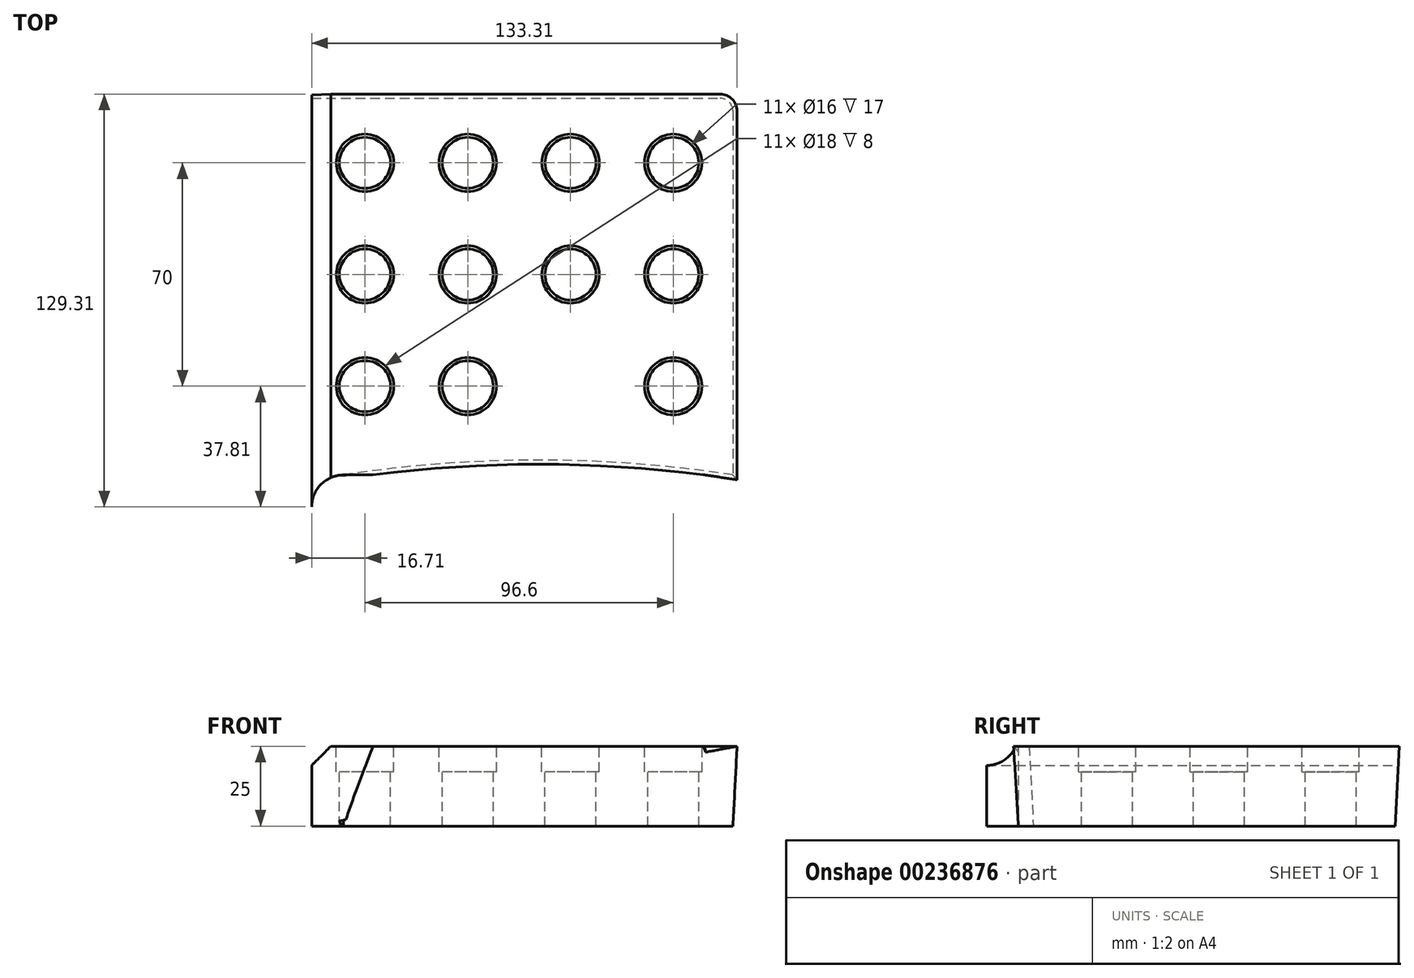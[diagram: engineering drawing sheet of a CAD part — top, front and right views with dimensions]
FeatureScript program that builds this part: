
annotation { "Feature Type Name" : "Feature", "Feature Type Description" : "" }
export const myFeature = defineFeature(function(context is Context, id is Id, definition is map)
    precondition{}
    {
        {
            var Q0;
            Q0=qCreatedBy(makeId("Top.planeOp"),FACE);
            var sketch = newSketch(context, id + "F0", { "sketchPlane" : qUnion([Q0])});
            skLineSegment(sketch, "E0.bottom", {"start": v(0, 0) * mm, "end": v(10, 0) * mm});
            skLineSegment(sketch, "E0.top", {"start": v(0, 118) * mm, "end": v(128, 118) * mm});
            skLineSegment(sketch, "E0.left", {"start": v(0, 0) * mm, "end": v(0, 118) * mm});
            skLineSegment(sketch, "E0.right", {"start": v(132, 0) * mm, "end": v(132, 114) * mm});
            skPoint(sketch, "E1.visualSharp", {"position": v(132, 118) * mm});
            skArc(sketch, "E1.filletArc", {"start": v(132, 114) * mm, "mid": v(130.83, 116.83) * mm, "end": v(128, 118) * mm});
            skLineSegment(sketch, "E2", {"start": v(0, 0) * mm, "end": v(10, 0) * mm, "construction": true});
            skArc(sketch, "E3", {"start": v(132, 0) * mm, "mid": v(71, 4.68) * mm, "end": v(10, 0) * mm});
            skSolve(sketch);
        }
        {
            var Q0;
            Q0 = qSketchRegion(id + "F0", true);
            extrude(context, id + "F1", {"entities" : qUnion([Q0]), "depth" : 25 * mm, "hasDraft" : true, "draftAngle" : 3 * degree});
        }
        {
            var Q0;
            Q0=qCreatedBy(makeId("Front.planeOp"),FACE);
            var sketch = newSketch(context, id + "F2", { "sketchPlane" : qUnion([Q0])});
            skLineSegment(sketch, "E4.0.0", {"start": v(0, 0) * mm, "end": v(0, 0) * mm});
            skLineSegment(sketch, "E4.0.1", {"start": v(0, 0) * mm, "end": v(133.31, 25) * mm});
            skLineSegment(sketch, "E4.0.2", {"start": v(-1.31, 25) * mm, "end": v(133.31, 25) * mm});
            skLineSegment(sketch, "E4.0.3", {"start": v(-1.31, 25) * mm, "end": v(0, 0) * mm});
            skSolve(sketch);
        }
        {
            var Q0;
            Q0 = qSketchRegion(id + "F2", true);
            extrude(context, id + "F3", {"entities" : qUnion([Q0]), "operationType" : NewBodyOperationType.REMOVE, "endBound" : BoundingType.THROUGH_ALL, "depth" : 25 * mm});
        }
        {
            var Q0;
            Q0=qCreatedBy(makeId("Right.planeOp"),FACE);
            var sketch = newSketch(context, id + "F4", { "sketchPlane" : qUnion([Q0])});
            skLineSegment(sketch, "E5.0.0", {"start": v(0, 0) * mm, "end": v(0, 25) * mm});
            skLineSegment(sketch, "E5.0.1", {"start": v(0, 25) * mm, "end": v(119.31, 25) * mm});
            skLineSegment(sketch, "E5.0.2", {"start": v(119.31, 25) * mm, "end": v(118, 0) * mm});
            skLineSegment(sketch, "E5.0.3", {"start": v(118, 0) * mm, "end": v(0, 0) * mm});
            skSolve(sketch);
        }
        {
            var Q0;
            Q0 = qSketchRegion(id + "F4", true);
            extrude(context, id + "F5", {"entities" : qUnion([Q0]), "operationType" : NewBodyOperationType.REMOVE, "endBound" : BoundingType.THROUGH_ALL, "oppositeDirection" : true, "depth" : 25 * mm});
        }
        {
            var Q0;
            Q0=qCreatedBy(makeId("Top.planeOp"),FACE);
            var sketch = newSketch(context, id + "F6", { "sketchPlane" : qUnion([Q0])});
            skLineSegment(sketch, "E6.bottom", {"start": v(10, 0) * mm, "end": v(10, 0) * mm});
            skLineSegment(sketch, "E6.left", {"start": v(0, -10) * mm, "end": v(0, -10) * mm});
            skPoint(sketch, "E7.visualSharp", {"position": v(0, 0) * mm});
            skArc(sketch, "E7.filletArc", {"start": v(10, 0) * mm, "mid": v(2.93, -2.93) * mm, "end": v(0, -10) * mm});
            skLineSegment(sketch, "E8", {"start": v(0, -10) * mm, "end": v(0, 0) * mm});
            skLineSegment(sketch, "E9", {"start": v(0, 0) * mm, "end": v(10, 0) * mm});
            skSolve(sketch);
        }
        {
            var Q0;
            Q0 = qSketchRegion(id + "F6", true);
            extrude(context, id + "F7", {"entities" : qUnion([Q0]), "operationType" : NewBodyOperationType.ADD, "depth" : 25 * mm});
        }
        {
            var Q0;
            Q0=makeQuery(id+"F7.boolean.opBoolean","MERGE",EDGE,{"derivedFrom":[makeQuery(id+"F5.boolean.opBoolean","COPY",EDGE,{"derivedFrom":makeQuery(id+"F5.opExtrude","CAP_EDGE",EDGE,{"disambiguationData":[OSD([sQuery(id+"F4.wireOp",EDGE,"E5.0.1")])],"isStart":true})}),makeQuery(id+"F7.opExtrude","CAP_EDGE",EDGE,{"disambiguationData":[OSD([sQuery(id+"F6.wireOp",EDGE,"E8")])],"isStart":false})]});
            chamfer(context, id + "F8", {"entities" : qUnion([Q0]), "width" : 6 * mm, "tangentPropagation" : true});
        }
        {
            var Q0;
            {var subQ1=sQuery(id+"F0.wireOp",EDGE,"E0.right");var subQ2=sQuery(id+"F2.wireOp",EDGE,"E4.0.1");Q0=makeQuery(id+"F3.boolean.opBoolean","COPY",FACE,{"disambiguationData":[TD([makeQuery(id+"F1.opExtrude","SWEPT_FACE",FACE,{"disambiguationData":[OSD([subQ1])]})])],"derivedFrom":makeQuery(id+"F3.opExtrude","SWEPT_FACE",FACE,{"disambiguationData":[OSD([subQ2])]})});}
            var sketch = newSketch(context, id + "F9", { "sketchPlane" : qUnion([Q0])});
            skLineSegment(sketch, "E10.0.0", {"start": v(135.63, -1.53) * mm, "end": v(135.63, 0) * mm});
            skLineSegment(sketch, "E10.0.1", {"start": v(135.63, 0) * mm, "end": v(125.6, 0) * mm});
            skEllipticalArc(sketch, "E10.0.2", {});
            const initialGuessF9  = {"E10.0.2": [0.06824448755918142, -0.39532138823999896, -1, 0, 0.40630219611644297, 0.39932148659949984, 4.545758140319845, 4.5707273626514375]};
            skSetInitialGuess(sketch, initialGuessF9);
            skSolve(sketch);
        }
        {
            var Q0;
            Q0 = qSketchRegion(id + "F9", true);
            var Q1;
            Q1=makeQuery(id+"F7.boolean.opBoolean","MERGE",FACE,{"derivedFrom":[makeQuery(id+"F1.opExtrude","CAP_FACE",FACE,{"disambiguationData":[OSD([sQuery(id+"F0.wireOp",EDGE,"E0.bottom"),sQuery(id+"F0.wireOp",EDGE,"E0.top"),sQuery(id+"F0.wireOp",EDGE,"E0.left"),sQuery(id+"F0.wireOp",EDGE,"E0.right"),sQuery(id+"F0.wireOp",EDGE,"E1.filletArc"),sQuery(id+"F0.wireOp",EDGE,"E3")])],"isStart":false}),makeQuery(id+"F7.opExtrude","CAP_FACE",FACE,{"disambiguationData":[OSD([sQuery(id+"F6.wireOp",EDGE,"E7.filletArc"),sQuery(id+"F6.wireOp",EDGE,"E8"),sQuery(id+"F6.wireOp",EDGE,"E9")])],"isStart":false})]});
            extrude(context, id + "F10", {"entities" : qUnion([Q0]), "operationType" : NewBodyOperationType.ADD, "endBound" : BoundingType.UP_TO_SURFACE, "endBoundEntityFace" : qUnion([Q1]), "depth" : 25 * mm, "offsetDistance" : 25 * mm});
        }
        {
            var Q0;
            Q0=makeQuery(id+"F7.boolean.opBoolean","MERGE",FACE,{"derivedFrom":[makeQuery(id+"F1.opExtrude","CAP_FACE",FACE,{"disambiguationData":[OSD([sQuery(id+"F0.wireOp",EDGE,"E0.bottom"),sQuery(id+"F0.wireOp",EDGE,"E0.top"),sQuery(id+"F0.wireOp",EDGE,"E0.left"),sQuery(id+"F0.wireOp",EDGE,"E0.right"),sQuery(id+"F0.wireOp",EDGE,"E1.filletArc")])],"isStart":false}),makeQuery(id+"F7.opExtrude","CAP_FACE",FACE,{"disambiguationData":[OSD([sQuery(id+"F6.wireOp",EDGE,"E7.filletArc"),sQuery(id+"F6.wireOp",EDGE,"E8"),sQuery(id+"F6.wireOp",EDGE,"E9")])],"isStart":false})]});
            var sketch = newSketch(context, id + "F11", { "sketchPlane" : qUnion([Q0])});
            skLineSegment(sketch, "E11", {"start": v(128, 119.31) * mm, "end": v(139.92, 119.31) * mm, "construction": true});
            skLineSegment(sketch, "E12", {"start": v(139.92, 119.31) * mm, "end": v(133.31, 114) * mm, "construction": true});
            skLineSegment(sketch, "E13", {"start": v(133.31, 114) * mm, "end": v(133.31, 119.31) * mm, "construction": true});
            skLineSegment(sketch, "E14.bottom", {"start": v(133.31, 119.31) * mm, "end": v(113.31, 119.31) * mm, "construction": true});
            skLineSegment(sketch, "E14.top", {"start": v(133.31, 97.81) * mm, "end": v(113.31, 97.81) * mm, "construction": true});
            skLineSegment(sketch, "E14.left", {"start": v(133.31, 119.31) * mm, "end": v(133.31, 97.81) * mm, "construction": true});
            skLineSegment(sketch, "E14.right", {"start": v(113.31, 119.31) * mm, "end": v(113.31, 97.81) * mm, "construction": true});
            skLineSegment(sketch, "E15.bottom", {"start": v(113.31, 97.81) * mm, "end": v(81.11, 97.81) * mm, "construction": true});
            skLineSegment(sketch, "E15.top", {"start": v(113.31, 62.81) * mm, "end": v(81.11, 62.81) * mm, "construction": true});
            skLineSegment(sketch, "E15.left", {"start": v(113.31, 97.81) * mm, "end": v(113.31, 62.81) * mm, "construction": true});
            skLineSegment(sketch, "E15.right", {"start": v(81.11, 97.81) * mm, "end": v(81.11, 62.81) * mm, "construction": true});
            skLineSegment(sketch, "E16.bottom", {"start": v(81.11, 97.81) * mm, "end": v(48.91, 97.81) * mm, "construction": true});
            skLineSegment(sketch, "E16.top", {"start": v(81.11, 62.81) * mm, "end": v(48.91, 62.81) * mm, "construction": true});
            skLineSegment(sketch, "E16.right", {"start": v(48.91, 97.81) * mm, "end": v(48.91, 62.81) * mm, "construction": true});
            skLineSegment(sketch, "E17.bottom", {"start": v(48.91, 97.81) * mm, "end": v(16.71, 97.81) * mm, "construction": true});
            skLineSegment(sketch, "E17.top", {"start": v(48.91, 62.81) * mm, "end": v(16.71, 62.81) * mm, "construction": true});
            skLineSegment(sketch, "E17.right", {"start": v(16.71, 97.81) * mm, "end": v(16.71, 62.81) * mm, "construction": true});
            skLineSegment(sketch, "E18.bottom", {"start": v(16.71, 62.81) * mm, "end": v(16.71, 62.81) * mm});
            skLineSegment(sketch, "E18.top", {"start": v(16.71, 27.81) * mm, "end": v(16.71, 27.81) * mm});
            skLineSegment(sketch, "E18.left", {"start": v(16.71, 62.81) * mm, "end": v(16.71, 27.81) * mm, "construction": true});
            skLineSegment(sketch, "E18.right", {"start": v(16.71, 62.81) * mm, "end": v(16.71, 27.81) * mm, "construction": true});
            skLineSegment(sketch, "E19.bottom", {"start": v(113.31, 62.81) * mm, "end": v(48.91, 62.81) * mm, "construction": true});
            skLineSegment(sketch, "E19.top", {"start": v(113.31, 27.81) * mm, "end": v(48.91, 27.81) * mm, "construction": true});
            skLineSegment(sketch, "E19.right", {"start": v(48.91, 62.81) * mm, "end": v(48.91, 27.81) * mm, "construction": true});
            skCircle(sketch, "E20", {"center": v(16.71, 97.81) * mm, "radius": 8 * mm});
            skCircle(sketch, "E21", {"center": v(48.91, 97.81) * mm, "radius": 9 * mm});
            skCircle(sketch, "E22", {"center": v(81.11, 97.81) * mm, "radius": 9 * mm});
            skCircle(sketch, "E23", {"center": v(113.31, 97.81) * mm, "radius": 9 * mm});
            skCircle(sketch, "E24", {"center": v(113.31, 62.81) * mm, "radius": 9 * mm});
            skCircle(sketch, "E25", {"center": v(81.11, 62.81) * mm, "radius": 9 * mm});
            skCircle(sketch, "E26", {"center": v(48.91, 62.81) * mm, "radius": 9 * mm});
            skCircle(sketch, "E27", {"center": v(16.71, 62.81) * mm, "radius": 9 * mm});
            skCircle(sketch, "E28", {"center": v(16.71, 27.81) * mm, "radius": 9 * mm});
            skCircle(sketch, "E29", {"center": v(48.91, 27.81) * mm, "radius": 9 * mm});
            skCircle(sketch, "E30", {"center": v(48.91, 27.81) * mm, "radius": 8 * mm});
            skCircle(sketch, "E31", {"center": v(113.31, 62.81) * mm, "radius": 8 * mm});
            skCircle(sketch, "E32", {"center": v(81.11, 62.81) * mm, "radius": 8 * mm});
            skCircle(sketch, "E33", {"center": v(48.91, 62.81) * mm, "radius": 8 * mm});
            skCircle(sketch, "E34", {"center": v(16.71, 62.81) * mm, "radius": 8 * mm});
            skCircle(sketch, "E35", {"center": v(16.71, 27.81) * mm, "radius": 8 * mm});
            skCircle(sketch, "E36", {"center": v(48.91, 97.81) * mm, "radius": 8 * mm});
            skCircle(sketch, "E37", {"center": v(16.71, 97.81) * mm, "radius": 9 * mm});
            skCircle(sketch, "E38", {"center": v(81.11, 97.81) * mm, "radius": 8 * mm});
            skCircle(sketch, "E39", {"center": v(113.31, 97.81) * mm, "radius": 8 * mm});
            skCircle(sketch, "E40", {"center": v(113.31, 27.81) * mm, "radius": 9 * mm});
            skCircle(sketch, "E41", {"center": v(113.31, 27.81) * mm, "radius": 8 * mm});
            skSolve(sketch);
        }
        {
            var Q0;
            Q0=makeQuery(id+"F11.imprint","IMPRINT",FACE,{"disambiguationData":[TD([[makeQuery(id+"F11.imprint","IMPRINT",EDGE,{"derivedFrom":sQuery(id+"F11.wireOp",EDGE,"E36")}),1.0]])]});
            var Q1;
            Q1=makeQuery(id+"F11.imprint","IMPRINT",FACE,{"disambiguationData":[TD([[makeQuery(id+"F11.imprint","IMPRINT",EDGE,{"derivedFrom":sQuery(id+"F11.wireOp",EDGE,"E38")}),1.0]])]});
            var Q2;
            Q2=makeQuery(id+"F11.imprint","IMPRINT",FACE,{"disambiguationData":[TD([[makeQuery(id+"F11.imprint","IMPRINT",EDGE,{"derivedFrom":sQuery(id+"F11.wireOp",EDGE,"E39")}),1.0]])]});
            var Q3;
            Q3=makeQuery(id+"F11.imprint","IMPRINT",FACE,{"disambiguationData":[TD([[makeQuery(id+"F11.imprint","IMPRINT",EDGE,{"derivedFrom":sQuery(id+"F11.wireOp",EDGE,"E31")}),1.0]])]});
            var Q4;
            Q4=makeQuery(id+"F11.imprint","IMPRINT",FACE,{"disambiguationData":[TD([[makeQuery(id+"F11.imprint","IMPRINT",EDGE,{"derivedFrom":sQuery(id+"F11.wireOp",EDGE,"E32")}),1.0]])]});
            var Q5;
            Q5=makeQuery(id+"F11.imprint","IMPRINT",FACE,{"disambiguationData":[TD([[makeQuery(id+"F11.imprint","IMPRINT",EDGE,{"derivedFrom":sQuery(id+"F11.wireOp",EDGE,"E33")}),1.0]])]});
            var Q6;
            Q6=makeQuery(id+"F11.imprint","IMPRINT",FACE,{"disambiguationData":[TD([[makeQuery(id+"F11.imprint","IMPRINT",EDGE,{"derivedFrom":sQuery(id+"F11.wireOp",EDGE,"E34")}),1.0]])]});
            var Q7;
            Q7=makeQuery(id+"F11.imprint","IMPRINT",FACE,{"disambiguationData":[TD([[makeQuery(id+"F11.imprint","IMPRINT",EDGE,{"derivedFrom":sQuery(id+"F11.wireOp",EDGE,"E35")}),1.0]])]});
            var Q8;
            Q8=makeQuery(id+"F11.imprint","IMPRINT",FACE,{"disambiguationData":[TD([[makeQuery(id+"F11.imprint","IMPRINT",EDGE,{"derivedFrom":sQuery(id+"F11.wireOp",EDGE,"E30")}),1.0]])]});
            var Q9;
            Q9=makeQuery(id+"F11.imprint","IMPRINT",FACE,{"disambiguationData":[TD([[makeQuery(id+"F11.imprint","IMPRINT",EDGE,{"derivedFrom":sQuery(id+"F11.wireOp",EDGE,"E41")}),1.0]])]});
            var Q10;
            Q10=makeQuery(id+"F11.imprint","IMPRINT",FACE,{"disambiguationData":[TD([[makeQuery(id+"F11.imprint","IMPRINT",EDGE,{"derivedFrom":sQuery(id+"F11.wireOp",EDGE,"E20")}),1.0]])]});
            extrude(context, id + "F12", {"entities" : qUnion([Q0, Q1, Q2, Q3, Q4, Q5, Q6, Q7, Q8, Q9, Q10]), "operationType" : NewBodyOperationType.REMOVE, "oppositeDirection" : true, "depth" : 25 * mm, "offsetDistance" : 25 * mm});
        }
        {
            var Q0;
            Q0=makeQuery(id+"F11.imprint","IMPRINT",FACE,{"disambiguationData":[TD([[makeQuery(id+"F11.imprint","IMPRINT",EDGE,{"derivedFrom":sQuery(id+"F11.wireOp",EDGE,"E20")}),1.0]])]});
            var Q1;
            Q1=makeQuery(id+"F11.imprint","IMPRINT",FACE,{"disambiguationData":[TD([[makeQuery(id+"F11.imprint","IMPRINT",EDGE,{"derivedFrom":sQuery(id+"F11.wireOp",EDGE,"E21")}),1.0]])]});
            var Q2;
            Q2=makeQuery(id+"F11.imprint","IMPRINT",FACE,{"disambiguationData":[TD([[makeQuery(id+"F11.imprint","IMPRINT",EDGE,{"derivedFrom":sQuery(id+"F11.wireOp",EDGE,"E27")}),1.0]])]});
            var Q3;
            Q3=makeQuery(id+"F11.imprint","IMPRINT",FACE,{"disambiguationData":[TD([[makeQuery(id+"F11.imprint","IMPRINT",EDGE,{"derivedFrom":sQuery(id+"F11.wireOp",EDGE,"E26")}),1.0]])]});
            var Q4;
            Q4=makeQuery(id+"F11.imprint","IMPRINT",FACE,{"disambiguationData":[TD([[makeQuery(id+"F11.imprint","IMPRINT",EDGE,{"derivedFrom":sQuery(id+"F11.wireOp",EDGE,"E28")}),1.0]])]});
            var Q5;
            Q5=makeQuery(id+"F11.imprint","IMPRINT",FACE,{"disambiguationData":[TD([[makeQuery(id+"F11.imprint","IMPRINT",EDGE,{"derivedFrom":sQuery(id+"F11.wireOp",EDGE,"E22")}),1.0]])]});
            var Q6;
            Q6=makeQuery(id+"F11.imprint","IMPRINT",FACE,{"disambiguationData":[TD([[makeQuery(id+"F11.imprint","IMPRINT",EDGE,{"derivedFrom":sQuery(id+"F11.wireOp",EDGE,"E25")}),1.0]])]});
            var Q7;
            Q7=makeQuery(id+"F11.imprint","IMPRINT",FACE,{"disambiguationData":[TD([[makeQuery(id+"F11.imprint","IMPRINT",EDGE,{"derivedFrom":sQuery(id+"F11.wireOp",EDGE,"E29")}),1.0]])]});
            var Q8;
            Q8=makeQuery(id+"F11.imprint","IMPRINT",FACE,{"disambiguationData":[TD([[makeQuery(id+"F11.imprint","IMPRINT",EDGE,{"derivedFrom":sQuery(id+"F11.wireOp",EDGE,"E24")}),1.0]])]});
            var Q9;
            Q9=makeQuery(id+"F11.imprint","IMPRINT",FACE,{"disambiguationData":[TD([[makeQuery(id+"F11.imprint","IMPRINT",EDGE,{"derivedFrom":sQuery(id+"F11.wireOp",EDGE,"E23")}),1.0]])]});
            var Q10;
            Q10=makeQuery(id+"F11.imprint","IMPRINT",FACE,{"disambiguationData":[TD([[makeQuery(id+"F11.imprint","IMPRINT",EDGE,{"derivedFrom":sQuery(id+"F11.wireOp",EDGE,"E40")}),1.0]])]});
            var Q11;
            Q11=makeQuery(id+"F11.imprint","IMPRINT",FACE,{"disambiguationData":[TD([[makeQuery(id+"F11.imprint","IMPRINT",EDGE,{"derivedFrom":sQuery(id+"F11.wireOp",EDGE,"E20")}),-1.0]])]});
            extrude(context, id + "F13", {"entities" : qUnion([Q0, Q1, Q2, Q3, Q4, Q5, Q6, Q7, Q8, Q9, Q10, Q11]), "operationType" : NewBodyOperationType.REMOVE, "oppositeDirection" : true, "depth" : 8 * mm, "offsetDistance" : 25 * mm});
        }
    });
